# Revit family: M_Valve_Balancing and Control_MEPcontent_Oventrop_Hydrocontrol VFN 10624 DN 200-300
name_source: partatom
category: Pipe Accessories
revit_build: Autodesk Revit 2015 (Build: 20140223_1515(x64)
units: mm (PartAtom-declared; Revit-internal decimal feet)

## types (3) — shared parameters
Angle = 60.00°
Angle 2 = 30.00°
Angle 3 = -60.00°
Article Description = Balancing valve with both ports flanged
Article Type = Hydrocontrol VFN 10624 DN 200-300
Black = Color RGB 35-35-35
Bronze = Color RGB 156-122-90
Content Supplier URL = www.mepcontent.eu
Custom = No
Description = Balancing valve with both ports flanged
EMCS Version = 2.0
ETIM Article Class = EC011463
Family Version = 10.14
Hb5 = 10 mm  [stored 0.0328084 ft]
Hlp1 = 56 mm  [stored 0.183727 ft]
IFCExportAs = IfcValveType
IFCExportType = PRESSUREREDUCING
Lgt1 = 2 mm  [stored 0.00656168 ft]
MEPcontent Class = VALVE_BALANCING
Manufacturer = Oventrop
Manufacturer URL = http://www.oventrop.de
Model = Hydrocontrol VFN 10624 DN 200-300
Pressure Drop = 0.0 Pa
Product Line = Oventrop
R1 = 9 mm  [stored 0.0295276 ft]
R2 = 10 mm  [stored 0.0328084 ft]
RegulatorRadius = 150 mm
Revit Version = 2015
URL = www.stabiplan.com
r1 = 2 mm  [stored 0.00656168 ft]
r2 = 3 mm  [stored 0.00984252 ft]

## per-type parameters (varying)
- DN 200: CurDst=67 mm; Dst1=68 mm; DstChk=68 mm; FlangeDiameter=340 mm; GTIN=4026755241167; H=473 mm; Hb1=460 mm; Hb2=290 mm; Hb3=48 mm; Hb4=110 mm  [stored 0.360892 ft]; Hb6=218 mm; Height=467 mm; Hlp2=22 mm  [stored 0.0721785 ft]; K=295 mm; L2=67 mm; Length=600 mm; Lgt2=20 mm  [stored 0.0656168 ft]; Lgt3=59 mm; Lgt4=217 mm; Manufacturer Art. No.=1062456; NominalDiameter=200 mm; NominalRadius=100 mm; OuterDiameter=219 mm; Rad1=148 mm; Rad2=170 mm  [stored 0.557743 ft]; Rad3=119 mm; Rad4=116 mm; Rad5=156 mm  [stored 0.511811 ft]; Rad6=146 mm  [stored 0.479003 ft]; Rad7=160 mm  [stored 0.524934 ft]; VDst=54 mm; VHth=126 mm
- DN 250: CurDst=81 mm; Dst1=91 mm; DstChk=91 mm; FlangeDiameter=405 mm; GTIN=4026755241174; H=486 mm; Hb1=475 mm; Hb2=292 mm; Hb3=49 mm; Hb4=111 mm; Hb6=220 mm; Height=480 mm; Hlp2=27 mm; K=355 mm; L2=81 mm; Length=730 mm; Lgt2=22 mm  [stored 0.0721785 ft]; Lgt3=68 mm; Lgt4=260 mm; Manufacturer Art. No.=1062457; NominalDiameter=250 mm; NominalRadius=125 mm; OuterDiameter=273 mm; Rad1=178 mm; Rad2=203 mm; Rad3=143 mm; Rad4=140 mm; Rad5=180 mm; Rad6=170 mm  [stored 0.557743 ft]; Rad7=184 mm; VDst=63 mm; VHth=150 mm
- DN 300: CurDst=94 mm; Dst1=101 mm; DstChk=101 mm; FlangeDiameter=460 mm; GTIN=4026755241181; H=521 mm; Hb1=515 mm; Hb2=318 mm; Hb3=53 mm; Hb4=121 mm; Hb6=250 mm; Height=515 mm; Hlp2=31 mm; K=410 mm; L2=94 mm; Length=850 mm; Lgt2=23 mm; Lgt3=77 mm; Lgt4=302 mm; Manufacturer Art. No.=1062458; NominalDiameter=300 mm; NominalRadius=150 mm; OuterDiameter=324 mm; Rad1=205 mm; Rad2=230 mm; Rad3=166 mm  [stored 0.544619 ft]; Rad4=163 mm  [stored 0.534777 ft]; Rad5=203 mm; Rad6=193 mm; Rad7=207 mm; VDst=72 mm; VHth=173 mm

note: [stored X ft] marks values corroborated as IEEE doubles in the binary element streams (Revit-internal decimal feet)

## geometry (parser evidence)
native form markers: Blend x2, Sweep x2
no freeform markers — native parametric forms only
